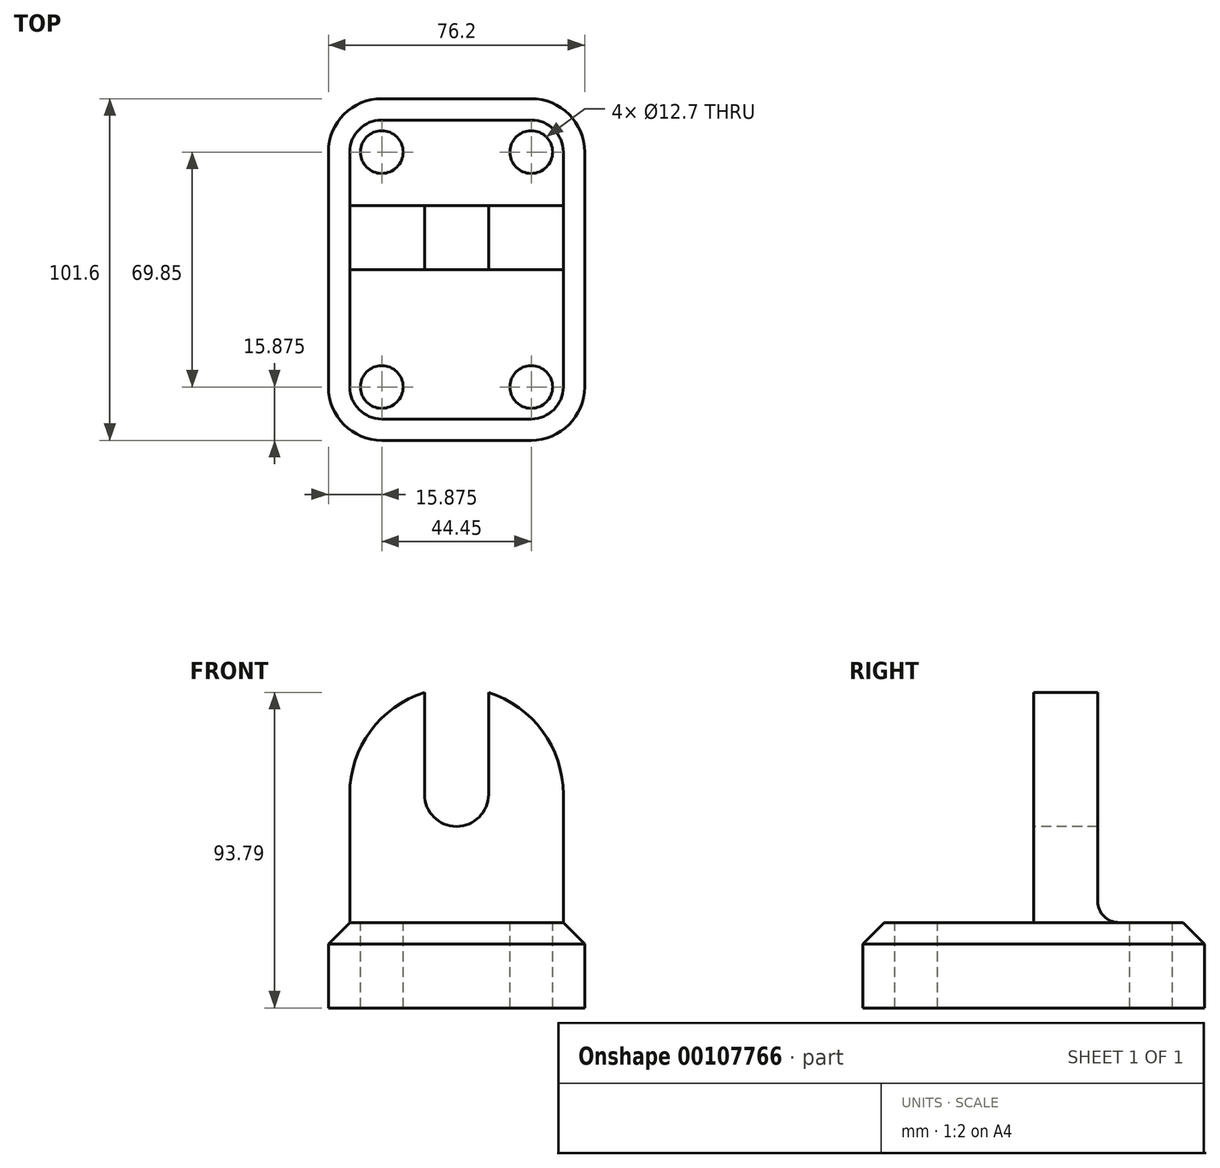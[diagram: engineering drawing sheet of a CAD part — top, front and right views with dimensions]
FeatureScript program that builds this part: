
annotation { "Feature Type Name" : "Feature", "Feature Type Description" : "" }
export const myFeature = defineFeature(function(context is Context, id is Id, definition is map)
    precondition{}
    {
        {
            var Q0;
            Q0=qCreatedBy(makeId("Top.planeOp"),FACE);
            var sketch = newSketch(context, id + "F0", { "sketchPlane" : qUnion([Q0])});
            skLineSegment(sketch, "E0.bottom", {"start": v(38.1, 50.8) * mm, "end": v(-38.1, 50.8) * mm});
            skLineSegment(sketch, "E0.top", {"start": v(38.1, -50.8) * mm, "end": v(-38.1, -50.8) * mm});
            skLineSegment(sketch, "E0.left", {"start": v(38.1, 50.8) * mm, "end": v(38.1, -50.8) * mm});
            skLineSegment(sketch, "E0.right", {"start": v(-38.1, 50.8) * mm, "end": v(-38.1, -50.8) * mm});
            skPoint(sketch, "E0.middle", {"position": v(0, 0) * mm});
            skSolve(sketch);
        }
        {
            var Q0;
            Q0=makeQuery(id+"F0.imprint","IMPRINT",FACE,{"disambiguationData":[TD([[makeQuery(id+"F0.imprint","IMPRINT",EDGE,{"derivedFrom":sQuery(id+"F0.wireOp",EDGE,"E0.bottom")}),1.0]])]});
            extrude(context, id + "F1", {"entities" : qUnion([Q0]), "depth" : 25.4 * mm});
        }
        {
            var Q0;
            Q0=makeQuery(id+"F1.opExtrude","CAP_FACE",FACE,{"disambiguationData":[OSD([sQuery(id+"F0.wireOp",EDGE,"E0.bottom"),sQuery(id+"F0.wireOp",EDGE,"E0.top"),sQuery(id+"F0.wireOp",EDGE,"E0.left"),sQuery(id+"F0.wireOp",EDGE,"E0.right")])],"isStart":false});
            var sketch = newSketch(context, id + "F2", { "sketchPlane" : qUnion([Q0])});
            skCircle(sketch, "E1", {"center": v(22.23, 34.93) * mm, "radius": 6.35 * mm});
            skCircle(sketch, "E2", {"center": v(-22.22, 34.93) * mm, "radius": 6.35 * mm});
            skCircle(sketch, "E3", {"center": v(-22.23, -34.92) * mm, "radius": 6.35 * mm});
            skLineSegment(sketch, "E4.top", {"start": v(-38.1, 0) * mm, "end": v(38.1, 0) * mm});
            skLineSegment(sketch, "E4.left", {"start": v(-38.1, -50.8) * mm, "end": v(-38.1, 0) * mm});
            skLineSegment(sketch, "E4.right", {"start": v(38.1, -50.8) * mm, "end": v(38.1, 0) * mm});
            skLineSegment(sketch, "E5.bottom", {"start": v(-38.1, 50.8) * mm, "end": v(38.1, 50.8) * mm});
            skLineSegment(sketch, "E5.top", {"start": v(-38.1, 19.05) * mm, "end": v(38.1, 19.05) * mm});
            skLineSegment(sketch, "E5.left", {"start": v(-38.1, 50.8) * mm, "end": v(-38.1, 19.05) * mm});
            skLineSegment(sketch, "E5.right", {"start": v(38.1, 50.8) * mm, "end": v(38.1, 19.05) * mm});
            skCircle(sketch, "E6", {"center": v(22.22, -34.92) * mm, "radius": 6.35 * mm});
            skLineSegment(sketch, "E7.left", {"start": v(-38.1, 19.05) * mm, "end": v(-38.1, 0) * mm});
            skLineSegment(sketch, "E7.right", {"start": v(38.1, 19.05) * mm, "end": v(38.1, 0) * mm});
            skSolve(sketch);
        }
        {
            var Q0;
            Q0=makeQuery(id+"F1.opExtrude","SWEPT_EDGE",EDGE,{"disambiguationData":[OSD([sQuery(id+"F0.wireOp",EDGE,"E0.bottom"),sQuery(id+"F0.wireOp",EDGE,"E0.left")])]});
            var Q1;
            Q1=makeQuery(id+"F1.opExtrude","SWEPT_EDGE",EDGE,{"disambiguationData":[OSD([sQuery(id+"F0.wireOp",EDGE,"E0.bottom"),sQuery(id+"F0.wireOp",EDGE,"E0.right")])]});
            var Q2;
            Q2=makeQuery(id+"F1.opExtrude","SWEPT_EDGE",EDGE,{"disambiguationData":[OSD([sQuery(id+"F0.wireOp",EDGE,"E0.top"),sQuery(id+"F0.wireOp",EDGE,"E0.right")])]});
            var Q3;
            Q3=makeQuery(id+"F1.opExtrude","SWEPT_EDGE",EDGE,{"disambiguationData":[OSD([sQuery(id+"F0.wireOp",EDGE,"E0.top"),sQuery(id+"F0.wireOp",EDGE,"E0.left")])]});
            fillet(context, id + "F3", {"entities" : qUnion([Q0, Q1, Q2, Q3]), "radius" : 15.88 * mm, "tangentPropagation" : true, "allowEdgeOverflow" : false});
        }
        {
            var Q0;
            Q0=makeQuery(id+"F1.opExtrude","CAP_FACE",FACE,{"disambiguationData":[OSD([sQuery(id+"F0.wireOp",EDGE,"E0.bottom"),sQuery(id+"F0.wireOp",EDGE,"E0.top"),sQuery(id+"F0.wireOp",EDGE,"E0.left"),sQuery(id+"F0.wireOp",EDGE,"E0.right")])],"isStart":false});
            chamfer(context, id + "F4", {"entities" : qUnion([Q0]), "width" : 6.35 * mm, "tangentPropagation" : true});
        }
        {
            var Q0;
            Q0=sQuery(id+"F2.wireOp",VERTEX,"E2.center");
            var Q1;
            Q1=sQuery(id+"F2.wireOp",VERTEX,"E1.center");
            var Q2;
            Q2=sQuery(id+"F2.wireOp",VERTEX,"E6.center");
            var Q3;
            Q3=sQuery(id+"F2.wireOp",VERTEX,"E3.center");
            var Q4;
            Q4=makeQuery(id+"F1.opExtrude","SWEPT_BODY",BODY,{"disambiguationData":[OSD([sQuery(id+"F0.wireOp",EDGE,"E0.bottom"),sQuery(id+"F0.wireOp",EDGE,"E0.top"),sQuery(id+"F0.wireOp",EDGE,"E0.left"),sQuery(id+"F0.wireOp",EDGE,"E0.right")])]});
            hole(context, id + "F5", {"style" : HoleStyle.SIMPLE, "endStyle" : HoleEndStyle.THROUGH, "holeDiameter" : 12.7 * mm, "locations" : qUnion([Q0, Q1, Q2, Q3]), "scope" : qUnion([Q4]), "isTappedThrough" : true});
        }
        {
            var Q0;
            Q0=makeQuery(id+"F2.imprint","IMPRINT",FACE,{"disambiguationData":[TD([[makeQuery(id+"F2.imprint","IMPRINT",EDGE,{"derivedFrom":sQuery(id+"F2.wireOp",EDGE,"E5.top")}),-1.0]])]});
            extrude(context, id + "F6", {"entities" : qUnion([Q0]), "operationType" : NewBodyOperationType.ADD, "depth" : 69.85 * mm});
        }
        {
            var Q0;
            Q0=makeQuery(id+"F6.opExtrude","SWEPT_FACE",FACE,{"disambiguationData":[OSD([sQuery(id+"F2.wireOp",EDGE,"E4.top")])]});
            var sketch = newSketch(context, id + "F7", { "sketchPlane" : qUnion([Q0])});
            skLineSegment(sketch, "E8.bottom", {"start": v(-31.75, 25.4) * mm, "end": v(-38.1, 25.4) * mm});
            skLineSegment(sketch, "E8.top", {"start": v(-31.75, 95.25) * mm, "end": v(-38.1, 95.25) * mm});
            skLineSegment(sketch, "E8.left", {"start": v(-31.75, 25.4) * mm, "end": v(-31.75, 95.25) * mm});
            skLineSegment(sketch, "E8.right", {"start": v(-38.1, 25.4) * mm, "end": v(-38.1, 95.25) * mm});
            skLineSegment(sketch, "E9.bottom", {"start": v(31.75, 25.4) * mm, "end": v(38.1, 25.4) * mm});
            skLineSegment(sketch, "E9.top", {"start": v(31.75, 95.25) * mm, "end": v(38.1, 95.25) * mm});
            skLineSegment(sketch, "E9.left", {"start": v(31.75, 25.4) * mm, "end": v(31.75, 95.25) * mm});
            skLineSegment(sketch, "E9.right", {"start": v(38.1, 25.4) * mm, "end": v(38.1, 95.25) * mm});
            skSolve(sketch);
        }
        {
            var Q0;
            Q0=qSketchRegion(id+"F7",true);
            extrude(context, id + "F8", {"entities" : qUnion([Q0]), "operationType" : NewBodyOperationType.REMOVE, "oppositeDirection" : true, "depth" : 19.05 * mm});
        }
        {
            var Q0;
            Q0=makeQuery(id+"F6.opExtrude","SWEPT_FACE",FACE,{"disambiguationData":[OSD([sQuery(id+"F2.wireOp",EDGE,"E4.top")])]});
            var sketch = newSketch(context, id + "F9", { "sketchPlane" : qUnion([Q0])});
            skLineSegment(sketch, "E10", {"start": v(0, 0) * mm, "end": v(0, 63.5) * mm});
            skCircle(sketch, "E11", {"center": v(0, 63.5) * mm, "radius": 9.53 * mm});
            skCircle(sketch, "E12", {"center": v(0, 63.5) * mm, "radius": 31.75 * mm});
            skLineSegment(sketch, "E13", {"start": v(-9.53, 63.5) * mm, "end": v(-9.53, 95.25) * mm});
            skLineSegment(sketch, "E14", {"start": v(9.53, 63.5) * mm, "end": v(9.53, 95.25) * mm});
            skSolve(sketch);
        }
        {
            var Q0;
            {var subQ0=sQuery(id+"F2.wireOp",EDGE,"E4.top");Q0=makeQuery(id+"F6.boolean.opBoolean","SPLIT",EDGE,{"disambiguationData":[topologyDisambiguationEdgeConnected([makeQuery(id+"F1.opExtrude","CAP_FACE",FACE,{"disambiguationData":[OSD([sQuery(id+"F0.wireOp",EDGE,"E0.bottom"),sQuery(id+"F0.wireOp",EDGE,"E0.top"),sQuery(id+"F0.wireOp",EDGE,"E0.left"),sQuery(id+"F0.wireOp",EDGE,"E0.right")])],"isStart":false}),makeQuery(id+"F6.opExtrude","SWEPT_FACE",FACE,{"disambiguationData":[OSD([subQ0])]})])],"derivedFrom":makeQuery(id+"F6.opExtrude","CAP_EDGE",EDGE,{"disambiguationData":[OSD([subQ0])],"isStart":true})});}
            var Q1;
            {var subQ0=sQuery(id+"F2.wireOp",EDGE,"E5.top");Q1=makeQuery(id+"F6.boolean.opBoolean","SPLIT",EDGE,{"disambiguationData":[topologyDisambiguationEdgeConnected([makeQuery(id+"F1.opExtrude","CAP_FACE",FACE,{"disambiguationData":[OSD([sQuery(id+"F0.wireOp",EDGE,"E0.bottom"),sQuery(id+"F0.wireOp",EDGE,"E0.top"),sQuery(id+"F0.wireOp",EDGE,"E0.left"),sQuery(id+"F0.wireOp",EDGE,"E0.right")])],"isStart":false}),makeQuery(id+"F6.opExtrude","SWEPT_FACE",FACE,{"disambiguationData":[OSD([subQ0])]})])],"derivedFrom":makeQuery(id+"F6.opExtrude","CAP_EDGE",EDGE,{"disambiguationData":[OSD([subQ0])],"isStart":true})});}
            fillet(context, id + "F10", {"entities" : qUnion([Q0, Q1]), "radius" : 6.35 * mm, "tangentPropagation" : true, "allowEdgeOverflow" : false});
        }
        {
            var Q0;
            {var subQ0=sQuery(id+"F9.wireOp",EDGE,"E13");var subQ1=sQuery(id+"F9.wireOp",EDGE,"E12");var subQ2=makeQuery(id+"F9.imprint","INTERSECT",VERTEX,{"derivedFrom":[subQ1,subQ0]});Q0=makeQuery(id+"F9.imprint","IMPRINT",FACE,{"disambiguationData":[TD([[makeQuery(id+"F9.imprint","IMPRINT",EDGE,{"disambiguationData":[TD([[subQ2,1.0]])],"derivedFrom":subQ1}),-1.0]])]});}
            var Q1;
            {var subQ0=sQuery(id+"F9.wireOp",EDGE,"E14");var subQ1=sQuery(id+"F9.wireOp",EDGE,"E12");var subQ2=makeQuery(id+"F9.imprint","INTERSECT",VERTEX,{"derivedFrom":[subQ1,subQ0]});Q1=makeQuery(id+"F9.imprint","IMPRINT",FACE,{"disambiguationData":[TD([[makeQuery(id+"F9.imprint","IMPRINT",EDGE,{"disambiguationData":[TD([[subQ2,-1.0]])],"derivedFrom":subQ1}),-1.0]])]});}
            var Q2;
            {var subQ0=sQuery(id+"F9.wireOp",EDGE,"E13");var subQ1=sQuery(id+"F9.wireOp",EDGE,"E12");var subQ2=makeQuery(id+"F9.imprint","INTERSECT",VERTEX,{"derivedFrom":[subQ1,subQ0]});Q2=makeQuery(id+"F9.imprint","IMPRINT",FACE,{"disambiguationData":[TD([[makeQuery(id+"F9.imprint","IMPRINT",EDGE,{"disambiguationData":[TD([[subQ2,-1.0]])],"derivedFrom":subQ1}),-1.0]])]});}
            var Q3;
            {var subQ0=sQuery(id+"F9.wireOp",EDGE,"E14");var subQ1=sQuery(id+"F9.wireOp",EDGE,"E12");var subQ2=makeQuery(id+"F9.imprint","INTERSECT",VERTEX,{"derivedFrom":[subQ1,subQ0]});Q3=makeQuery(id+"F9.imprint","IMPRINT",FACE,{"disambiguationData":[TD([[makeQuery(id+"F9.imprint","IMPRINT",EDGE,{"disambiguationData":[TD([[subQ2,1.0]])],"derivedFrom":subQ1}),-1.0]])]});}
            var Q4;
            {var subQ0=sQuery(id+"F9.wireOp",EDGE,"E13");var subQ1=sQuery(id+"F9.wireOp",EDGE,"E11");var subQ2=makeQuery(id+"F9.imprint","INTERSECT",VERTEX,{"derivedFrom":[subQ1,subQ0]});Q4=makeQuery(id+"F9.imprint","IMPRINT",FACE,{"disambiguationData":[TD([[makeQuery(id+"F9.imprint","IMPRINT",EDGE,{"disambiguationData":[TD([[subQ2,1.0]])],"derivedFrom":subQ1}),-1.0]])]});}
            var Q5;
            {var subQ0=sQuery(id+"F9.wireOp",EDGE,"E11");var subQ1=makeQuery(id+"F9.imprint","INTERSECT",VERTEX,{"derivedFrom":[subQ0,sQuery(id+"F9.wireOp",EDGE,"E13")]});Q5=makeQuery(id+"F9.imprint","IMPRINT",FACE,{"disambiguationData":[TD([[makeQuery(id+"F9.imprint","IMPRINT",EDGE,{"disambiguationData":[TD([[subQ1,1.0]])],"derivedFrom":subQ0}),1.0]])]});}
            extrude(context, id + "F11", {"entities" : qUnion([Q0, Q1, Q2, Q3, Q4, Q5]), "operationType" : NewBodyOperationType.REMOVE, "oppositeDirection" : true, "depth" : 19.05 * mm});
        }
        {
            var Q0;
            {var subQ0=sQuery(id+"F9.wireOp",EDGE,"E13");var subQ1=sQuery(id+"F9.wireOp",EDGE,"E11");var subQ2=makeQuery(id+"F9.imprint","INTERSECT",VERTEX,{"derivedFrom":[subQ1,subQ0]});Q0=makeQuery(id+"F9.imprint","IMPRINT",FACE,{"disambiguationData":[TD([[makeQuery(id+"F9.imprint","IMPRINT",EDGE,{"disambiguationData":[TD([[subQ2,1.0]])],"derivedFrom":subQ1}),-1.0]])]});}
            var Q1;
            {var subQ0=sQuery(id+"F9.wireOp",EDGE,"E11");var subQ1=makeQuery(id+"F9.imprint","INTERSECT",VERTEX,{"derivedFrom":[subQ0,sQuery(id+"F9.wireOp",EDGE,"E13")]});Q1=makeQuery(id+"F9.imprint","IMPRINT",FACE,{"disambiguationData":[TD([[makeQuery(id+"F9.imprint","IMPRINT",EDGE,{"disambiguationData":[TD([[subQ1,1.0]])],"derivedFrom":subQ0}),1.0]])]});}
            extrude(context, id + "F12", {"entities" : qUnion([Q0, Q1]), "operationType" : NewBodyOperationType.REMOVE, "oppositeDirection" : true, "depth" : 19.05 * mm});
        }
    });
